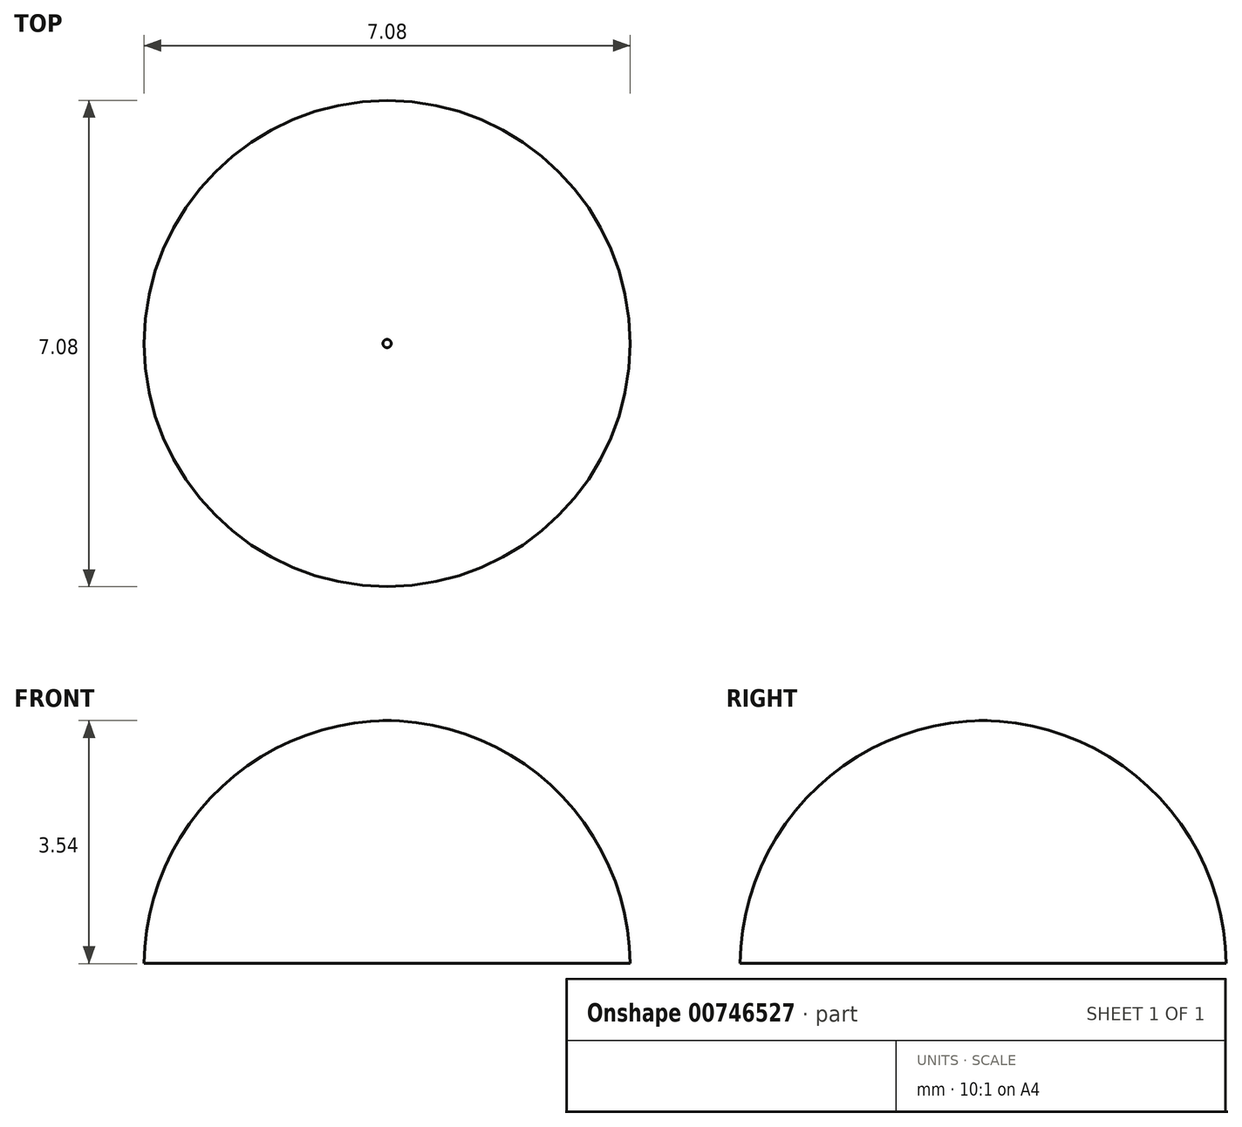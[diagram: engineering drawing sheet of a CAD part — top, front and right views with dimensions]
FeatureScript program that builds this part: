
annotation { "Feature Type Name" : "Feature", "Feature Type Description" : "" }
export const myFeature = defineFeature(function(context is Context, id is Id, definition is map)
    precondition{}
    {
        {
            var Q0;
            Q0=qCreatedBy(makeId("Right.planeOp"),FACE);
            var sketch = newSketch(context, id + "F0", { "sketchPlane" : qUnion([Q0])});
            skLineSegment(sketch, "E0", {"start": v(-42.06, 16.8) * mm, "end": v(-42.06, 20.34) * mm});
            skLineSegment(sketch, "E1", {"start": v(-42.06, 16.8) * mm, "end": v(-38.52, 16.8) * mm});
            skArc(sketch, "E2", {"start": v(-38.52, 16.8) * mm, "mid": v(-39.57, 19.3) * mm, "end": v(-42.06, 20.34) * mm});
            skSolve(sketch);
        }
        {
            var Q0;
            Q0=makeQuery(id+"F0.imprint","IMPRINT",FACE,{"disambiguationData":[TD([[makeQuery(id+"F0.imprint","IMPRINT",EDGE,{"derivedFrom":sQuery(id+"F0.wireOp",EDGE,"E0")}),-1.0]])]});
            var Q1;
            Q1=sQuery(id+"F0.wireOp",EDGE,"E0");
            revolve(context, id + "F1", {"surfaceOperationType" : NewSurfaceOperationType.NEW, "entities" : qUnion([Q0]), "axis" : qUnion([Q1]), "revolveType" : RevolveType.FULL});
        }
    });
